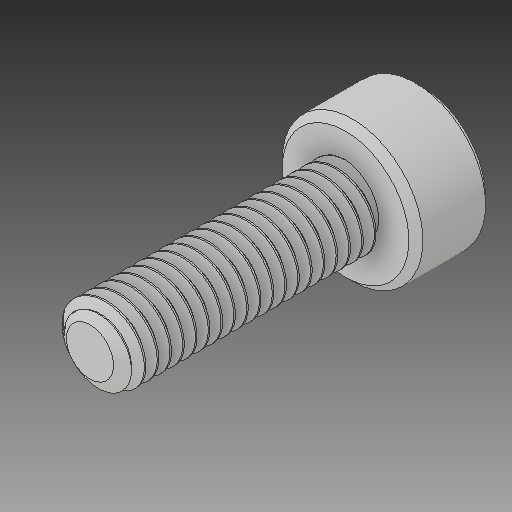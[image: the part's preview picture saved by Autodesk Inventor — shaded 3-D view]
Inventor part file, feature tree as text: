
AUTODESK INVENTOR PART (.ipt)
format: ipt  version: 2019.4 (Build 234330000, 330)  size: 729,600 bytes
history: native  units: in
note: dims shown in document units (in); Inventor stores cm internally (conversion verified against a paired STEP export)
features: chamfer x1
ambient origin geometry x8: Origin, YZ Plane, XZ Plane, XY Plane, X Axis, Y Axis, Z Axis, Center Point
bodies: Solid1 (feature_tree)
feature tree (1):
  chamfer  "Chamfer1"  [1 undecoded]
note: 1 required parameter value undecoded (feature->parameter linkage not recoverable at this tier; creation-order binding heuristic only, values carry confidence <= 0.55)
